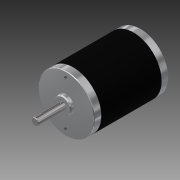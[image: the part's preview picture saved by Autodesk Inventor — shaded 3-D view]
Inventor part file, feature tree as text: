
AUTODESK INVENTOR PART (.ipt)
format: ipt  version: 2016 SP1 (Build 200210100, 210)  size: 165,888 bytes
history: native  units: in
note: dims shown in document units (in); Inventor stores cm internally (conversion verified against a paired STEP export)
features: thread x2, chamfer x1, other x1, imported_body x1
ambient origin geometry x8: Origin, YZ Plane, XZ Plane, XY Plane, X Axis, Y Axis, Z Axis, Center Point
bodies: Body1 (feature_tree)
feature tree (5):
  chamfer  "Chamfer3"  Distance=0.3937in
  other  "217-3371-STEP1"
  thread  "Thread1"  [1 undecoded]
  thread  "Thread2"  [1 undecoded]
  imported_body  "Base1"
note: 2 required parameter values undecoded (feature->parameter linkage not recoverable at this tier; creation-order binding heuristic only, values carry confidence <= 0.55)
